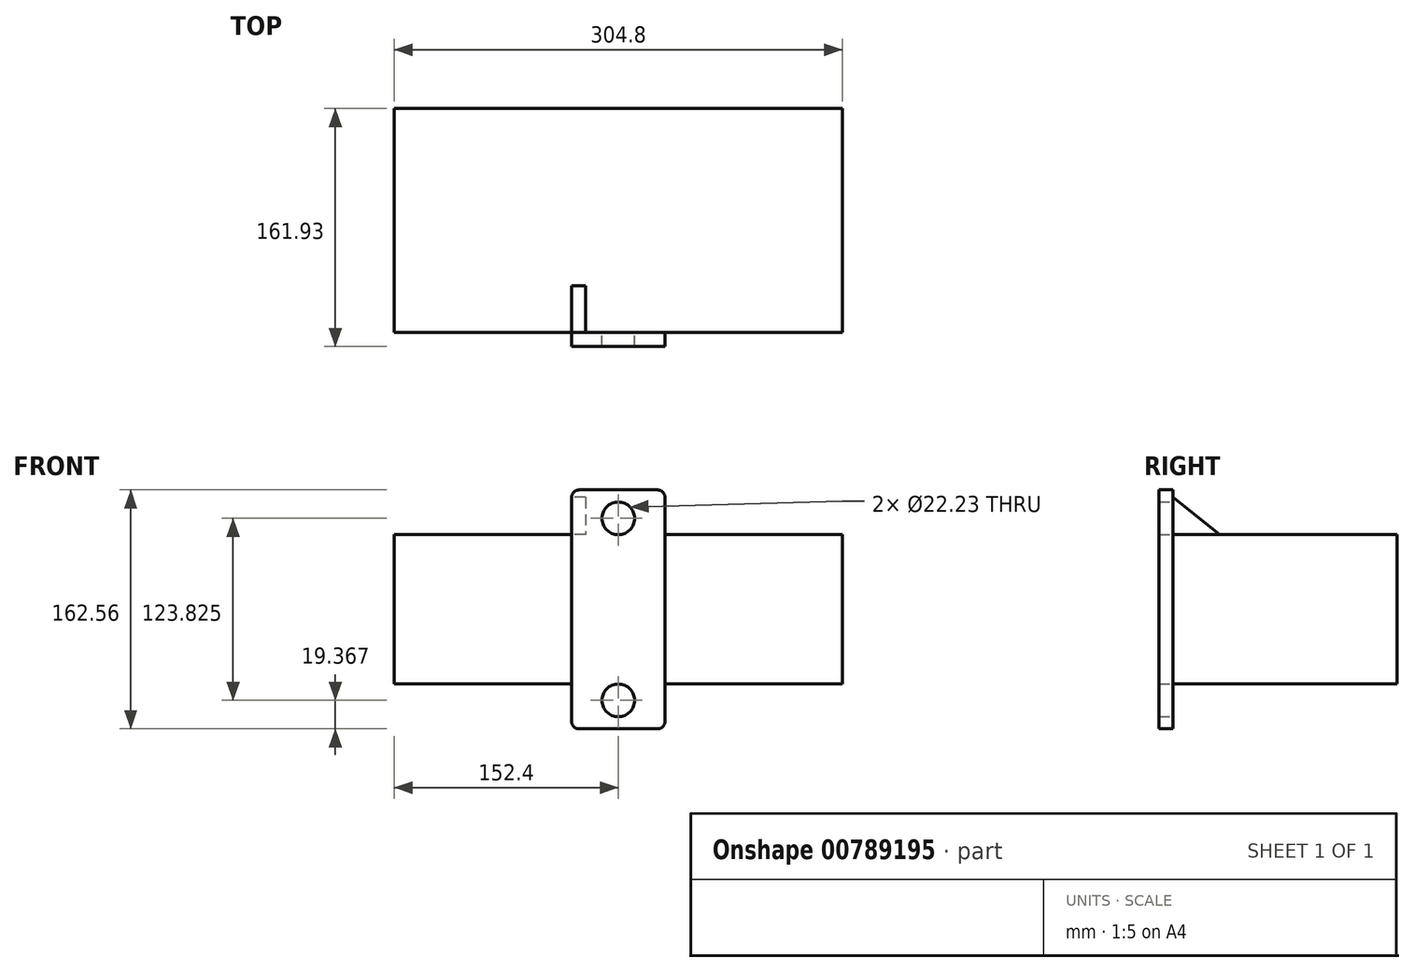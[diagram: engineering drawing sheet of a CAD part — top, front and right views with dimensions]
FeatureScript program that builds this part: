
annotation { "Feature Type Name" : "Feature", "Feature Type Description" : "" }
export const myFeature = defineFeature(function(context is Context, id is Id, definition is map)
    precondition{}
    {
        {
            var Q0;
            Q0=qCreatedBy(makeId("Right.planeOp"),FACE);
            var sketch = newSketch(context, id + "F0", { "sketchPlane" : qUnion([Q0])});
            skLineSegment(sketch, "E0.bottom", {"start": v(-76.2, 50.8) * mm, "end": v(76.2, 50.8) * mm});
            skLineSegment(sketch, "E0.top", {"start": v(-76.2, -50.8) * mm, "end": v(76.2, -50.8) * mm});
            skLineSegment(sketch, "E0.left", {"start": v(-76.2, 50.8) * mm, "end": v(-76.2, -50.8) * mm});
            skLineSegment(sketch, "E0.right", {"start": v(76.2, 50.8) * mm, "end": v(76.2, -50.8) * mm});
            skSolve(sketch);
        }
        {
            var Q0;
            Q0 = qSketchRegion(id + "F0", true);
            extrude(context, id + "F1", {"entities" : qUnion([Q0]), "endBound" : BoundingType.SYMMETRIC, "depth" : 304.8 * mm, "offsetDistance" : 25.4 * mm});
        }
        {
            var Q0;
            Q0=makeQuery(id+"F1.opExtrude","SWEPT_FACE",FACE,{"disambiguationData":[OSD([sQuery(id+"F0.wireOp",EDGE,"E0.left")])]});
            var sketch = newSketch(context, id + "F2", { "sketchPlane" : qUnion([Q0])});
            skCircle(sketch, "E1", {"center": v(0, 61.91) * mm, "radius": 11.11 * mm});
            skCircle(sketch, "E2", {"center": v(0, -61.91) * mm, "radius": 11.11 * mm});
            skLineSegment(sketch, "E3.bottom", {"start": v(-31.75, 81.28) * mm, "end": v(31.75, 81.28) * mm});
            skLineSegment(sketch, "E3.top", {"start": v(-31.75, -81.28) * mm, "end": v(31.75, -81.28) * mm});
            skLineSegment(sketch, "E3.left", {"start": v(-31.75, 81.28) * mm, "end": v(-31.75, -81.28) * mm});
            skLineSegment(sketch, "E3.right", {"start": v(31.75, 81.28) * mm, "end": v(31.75, -81.28) * mm});
            skSolve(sketch);
        }
        {
            var Q0;
            Q0 = qSketchRegion(id + "F2", true);
            extrude(context, id + "F3", {"entities" : qUnion([Q0]), "depth" : 9.52 * mm, "offsetDistance" : 25.4 * mm});
        }
        {
            var Q0;
            Q0=makeQuery(id+"F3.opExtrude","SWEPT_EDGE",EDGE,{"disambiguationData":[OSD([sQuery(id+"F2.wireOp",EDGE,"E3.bottom"),sQuery(id+"F2.wireOp",EDGE,"E3.left")])]});
            var Q1;
            Q1=makeQuery(id+"F3.opExtrude","SWEPT_EDGE",EDGE,{"disambiguationData":[OSD([sQuery(id+"F2.wireOp",EDGE,"E3.bottom"),sQuery(id+"F2.wireOp",EDGE,"E3.right")])]});
            var Q2;
            Q2=makeQuery(id+"F3.opExtrude","SWEPT_EDGE",EDGE,{"disambiguationData":[OSD([sQuery(id+"F2.wireOp",EDGE,"E3.top"),sQuery(id+"F2.wireOp",EDGE,"E3.left")])]});
            var Q3;
            Q3=makeQuery(id+"F3.opExtrude","SWEPT_EDGE",EDGE,{"disambiguationData":[OSD([sQuery(id+"F2.wireOp",EDGE,"E3.top"),sQuery(id+"F2.wireOp",EDGE,"E3.right")])]});
            fillet(context, id + "F4", {"entities" : qUnion([Q0, Q1, Q2, Q3]), "radius" : 5.08 * mm, "tangentPropagation" : true, "allowEdgeOverflow" : false});
        }
        {
            var Q0;
            Q0=makeQuery(id+"F3.opExtrude","SWEPT_FACE",FACE,{"disambiguationData":[OSD([sQuery(id+"F2.wireOp",EDGE,"E3.left")])]});
            var sketch = newSketch(context, id + "F5", { "sketchPlane" : qUnion([Q0])});
            skLineSegment(sketch, "E4", {"start": v(76.2, 50.8) * mm, "end": v(44.45, 50.8) * mm});
            skLineSegment(sketch, "E5", {"start": v(44.45, 50.8) * mm, "end": v(76.2, 76.2) * mm});
            skLineSegment(sketch, "E6", {"start": v(76.2, 76.2) * mm, "end": v(76.2, 50.8) * mm});
            skSolve(sketch);
        }
        {
            var Q0;
            Q0 = qSketchRegion(id + "F5", true);
            extrude(context, id + "F6", {"entities" : qUnion([Q0]), "oppositeDirection" : true, "depth" : 9.52 * mm, "offsetDistance" : 25.4 * mm});
        }
    });
